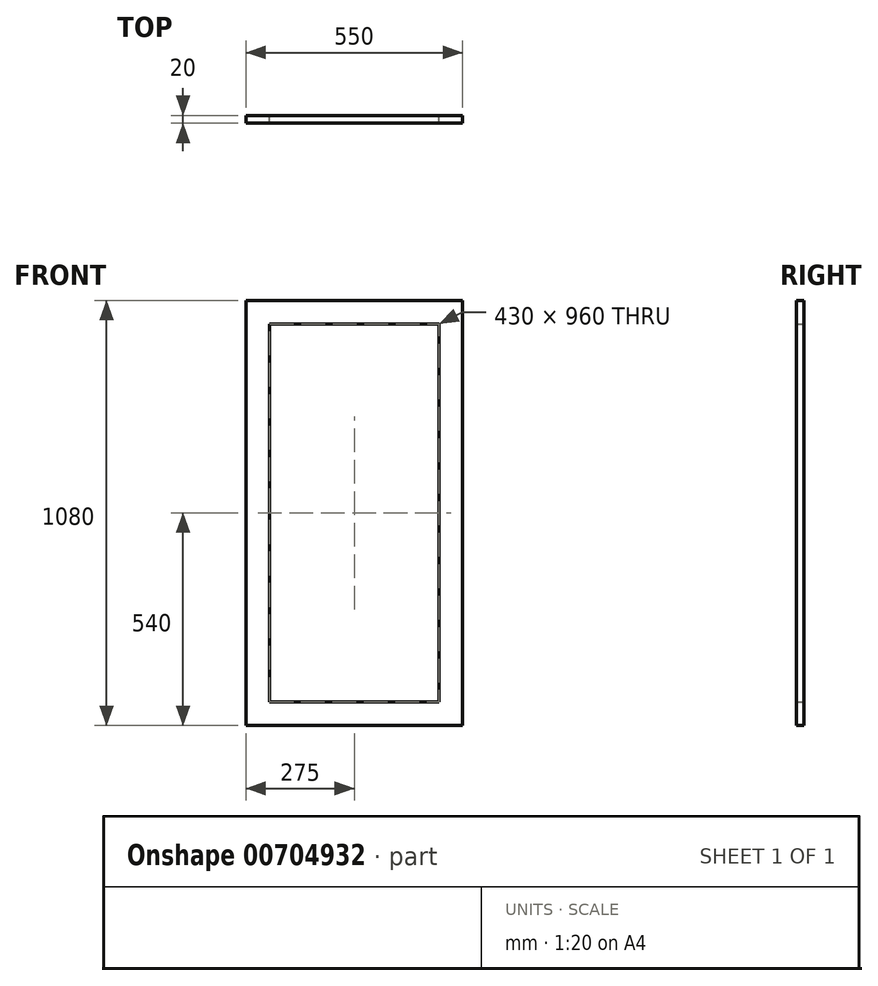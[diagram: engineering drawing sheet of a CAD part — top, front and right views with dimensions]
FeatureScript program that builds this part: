
annotation { "Feature Type Name" : "Feature", "Feature Type Description" : "" }
export const myFeature = defineFeature(function(context is Context, id is Id, definition is map)
    precondition{}
    {
        {
            var Q0;
            Q0=qCreatedBy(makeId("Front.planeOp"),FACE);
            var sketch = newSketch(context, id + "F0", { "sketchPlane" : qUnion([Q0])});
            skLineSegment(sketch, "E0.bottom", {"start": v(0, 0) * mm, "end": v(550, 0) * mm});
            skLineSegment(sketch, "E0.top", {"start": v(0, 1080) * mm, "end": v(550, 1080) * mm});
            skLineSegment(sketch, "E0.left", {"start": v(0, 0) * mm, "end": v(0, 1080) * mm});
            skLineSegment(sketch, "E0.right", {"start": v(550, 0) * mm, "end": v(550, 1080) * mm});
            skLineSegment(sketch, "E1.0", {"start": v(490, 60) * mm, "end": v(490, 1020) * mm});
            skLineSegment(sketch, "E1.1", {"start": v(60, 60) * mm, "end": v(490, 60) * mm});
            skLineSegment(sketch, "E1.2", {"start": v(60, 60) * mm, "end": v(60, 1020) * mm});
            skLineSegment(sketch, "E1.3", {"start": v(60, 1020) * mm, "end": v(490, 1020) * mm});
            skSolve(sketch);
        }
        {
            var Q0;
            Q0 = qSketchRegion(id + "F0", true);
            extrude(context, id + "F1", {"entities" : qUnion([Q0]), "depth" : 20 * mm, "offsetDistance" : 25 * mm});
        }
        {
            var Q0;
            Q0=makeQuery(id+"F0.imprint","IMPRINT",FACE,{"disambiguationData":[TD([[makeQuery(id+"F0.imprint","IMPRINT",EDGE,{"derivedFrom":sQuery(id+"F0.wireOp",EDGE,"E1.0")}),1.0]])]});
            extrude(context, id + "F2", {"entities" : qUnion([Q0]), "depth" : 1 * mm, "offsetDistance" : 25 * mm});
        }
    });
